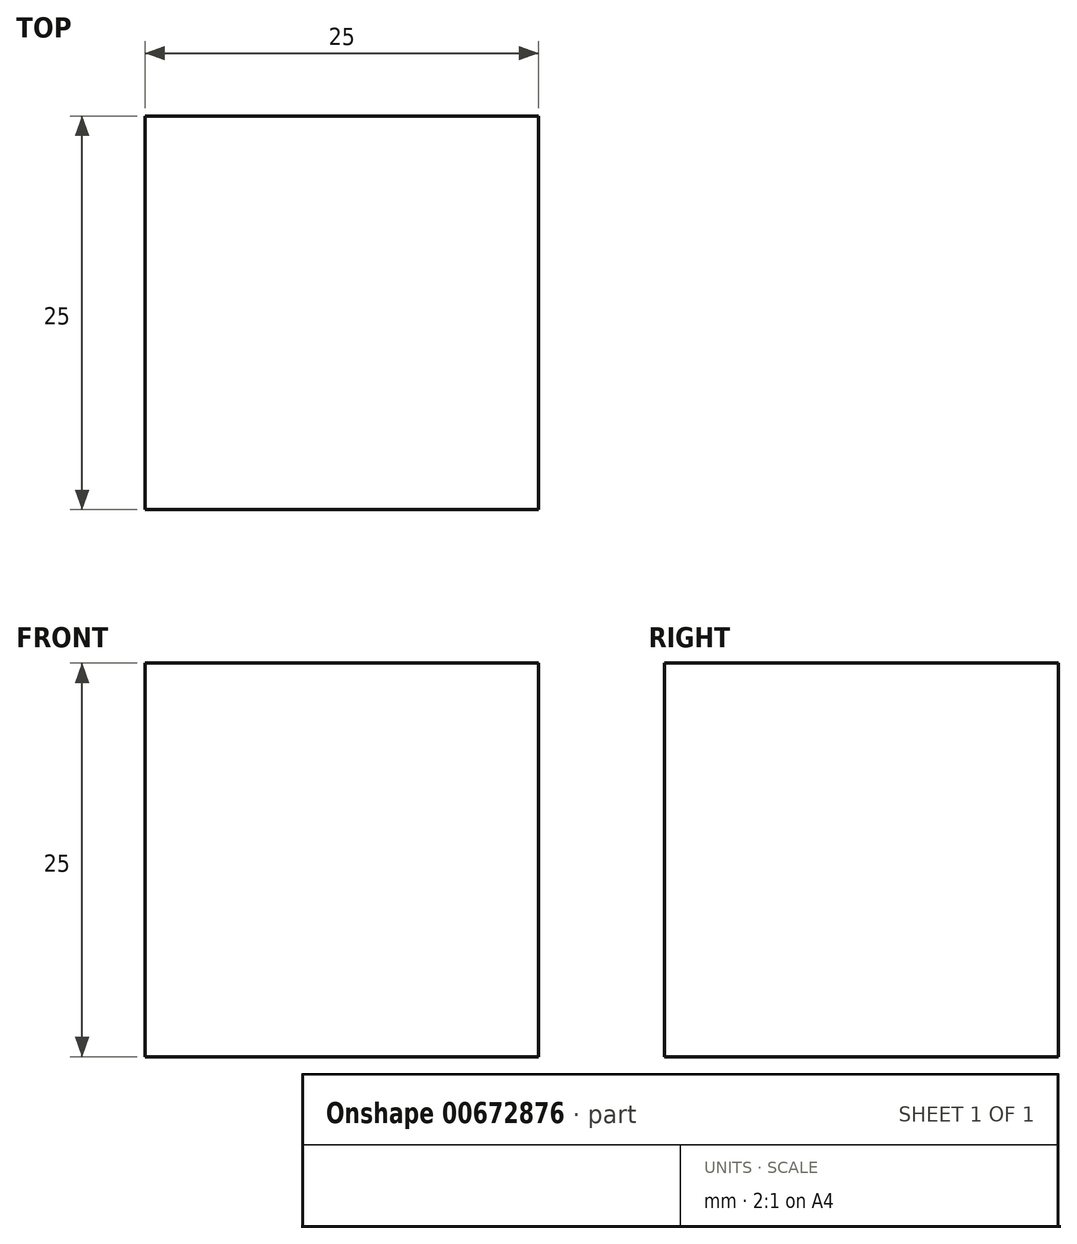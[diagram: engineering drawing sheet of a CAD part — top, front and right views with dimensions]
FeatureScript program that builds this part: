
annotation { "Feature Type Name" : "Feature", "Feature Type Description" : "" }
export const myFeature = defineFeature(function(context is Context, id is Id, definition is map)
    precondition{}
    {
        {
            var Q0;
            Q0=qCreatedBy(makeId("Top.planeOp"),FACE);
            var sketch = newSketch(context, id + "F0", { "sketchPlane" : qUnion([Q0])});
            skLineSegment(sketch, "E0.bottom", {"start": v(0, 0) * mm, "end": v(-25, 0) * mm});
            skLineSegment(sketch, "E0.top", {"start": v(0, 25) * mm, "end": v(-25, 25) * mm});
            skLineSegment(sketch, "E0.left", {"start": v(0, 0) * mm, "end": v(0, 25) * mm});
            skLineSegment(sketch, "E0.right", {"start": v(-25, 0) * mm, "end": v(-25, 25) * mm});
            skSolve(sketch);
        }
        {
            var Q0;
            Q0=makeQuery(id+"F0.imprint","IMPRINT",FACE,{"disambiguationData":[TD([[makeQuery(id+"F0.imprint","IMPRINT",EDGE,{"derivedFrom":sQuery(id+"F0.wireOp",EDGE,"E0.bottom")}),-1.0]])]});
            extrude(context, id + "F1", {"entities" : qUnion([Q0]), "depth" : 25 * mm, "offsetDistance" : 25 * mm});
        }
    });
